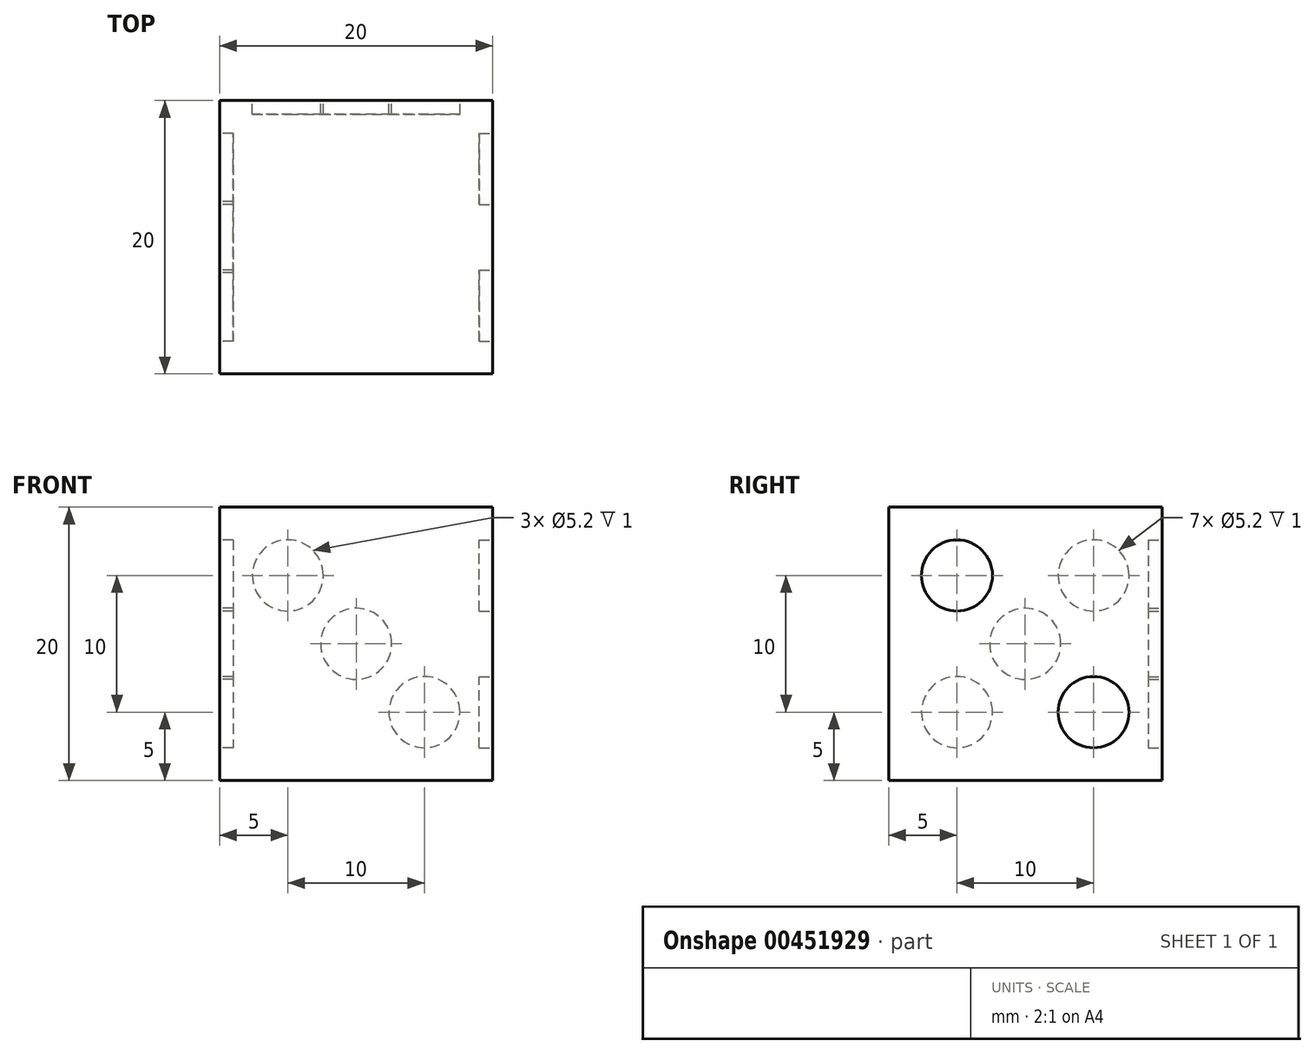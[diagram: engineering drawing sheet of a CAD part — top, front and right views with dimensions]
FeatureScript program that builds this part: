
annotation { "Feature Type Name" : "Feature", "Feature Type Description" : "" }
export const myFeature = defineFeature(function(context is Context, id is Id, definition is map)
    precondition{}
    {
        {
            var Q0;
            Q0=qCreatedBy(makeId("Front.planeOp"),FACE);
            var sketch = newSketch(context, id + "F0", { "sketchPlane" : qUnion([Q0])});
            skLineSegment(sketch, "E0.bottom", {"start": v(0, 0) * mm, "end": v(20, 0) * mm});
            skLineSegment(sketch, "E0.top", {"start": v(0, 20) * mm, "end": v(20, 20) * mm});
            skLineSegment(sketch, "E0.left", {"start": v(0, 0) * mm, "end": v(0, 20) * mm});
            skLineSegment(sketch, "E0.right", {"start": v(20, 0) * mm, "end": v(20, 20) * mm});
            skSolve(sketch);
        }
        {
            var Q0;
            Q0 = qSketchRegion(id + "F0", true);
            extrude(context, id + "F1", {"entities" : qUnion([Q0]), "depth" : 20 * mm});
        }
        {
            var Q0;
            Q0=makeQuery(id+"F1.opExtrude","SWEPT_FACE",FACE,{"disambiguationData":[OSD([sQuery(id+"F0.wireOp",EDGE,"E0.left")])]});
            var sketch = newSketch(context, id + "F2", { "sketchPlane" : qUnion([Q0])});
            skLineSegment(sketch, "E1", {"start": v(0, 20) * mm, "end": v(20, 0) * mm, "construction": true});
            skLineSegment(sketch, "E2", {"start": v(20, 0) * mm, "end": v(20, 20) * mm, "construction": true});
            skLineSegment(sketch, "E3", {"start": v(20, 20) * mm, "end": v(0, 0) * mm, "construction": true});
            skLineSegment(sketch, "E4", {"start": v(0, 10) * mm, "end": v(20, 10) * mm, "construction": true});
            skLineSegment(sketch, "E5", {"start": v(10, 20) * mm, "end": v(10, 0) * mm, "construction": true});
            skCircle(sketch, "E6", {"center": v(10, 10) * mm, "radius": 2.6 * mm});
            skCircle(sketch, "E7", {"center": v(5, 15) * mm, "radius": 2.6 * mm});
            skCircle(sketch, "E8.MirrorC", {"center": v(15, 15) * mm, "radius": 2.6 * mm});
            skCircle(sketch, "E9.MirrorC", {"center": v(15, 5) * mm, "radius": 2.6 * mm});
            skCircle(sketch, "E10.MirrorC", {"center": v(5, 5) * mm, "radius": 2.6 * mm});
            skSolve(sketch);
        }
        {
            var Q0;
            Q0 = qSketchRegion(id + "F2", true);
            extrude(context, id + "F3", {"entities" : qUnion([Q0]), "operationType" : NewBodyOperationType.REMOVE, "oppositeDirection" : true, "depth" : 1 * mm});
        }
        {
            var Q0;
            Q0=makeQuery(id+"F1.opExtrude","SWEPT_FACE",FACE,{"disambiguationData":[OSD([sQuery(id+"F0.wireOp",EDGE,"E0.right")])]});
            var sketch = newSketch(context, id + "F4", { "sketchPlane" : qUnion([Q0])});
            skLineSegment(sketch, "E11", {"start": v(0, 20) * mm, "end": v(-20, 0) * mm, "construction": true});
            skLineSegment(sketch, "E12", {"start": v(-20, 20) * mm, "end": v(0, 0) * mm, "construction": true});
            skLineSegment(sketch, "E13", {"start": v(-10, 20) * mm, "end": v(-10, 0) * mm, "construction": true});
            skLineSegment(sketch, "E14", {"start": v(-20, 10) * mm, "end": v(0, 10) * mm, "construction": true});
            skCircle(sketch, "E15", {"center": v(-15, 15) * mm, "radius": 2.6 * mm});
            skCircle(sketch, "E16.MirrorC", {"center": v(-5, 5) * mm, "radius": 2.6 * mm});
            skSolve(sketch);
        }
        {
            var Q0;
            Q0 = qSketchRegion(id + "F4", true);
            extrude(context, id + "F5", {"entities" : qUnion([Q0]), "operationType" : NewBodyOperationType.REMOVE, "oppositeDirection" : true, "depth" : 1 * mm});
        }
        {
            var Q0;
            Q0=makeQuery(id+"F1.opExtrude","CAP_FACE",FACE,{"disambiguationData":[OSD([sQuery(id+"F0.wireOp",EDGE,"E0.bottom"),sQuery(id+"F0.wireOp",EDGE,"E0.top"),sQuery(id+"F0.wireOp",EDGE,"E0.left"),sQuery(id+"F0.wireOp",EDGE,"E0.right")])],"isStart":true});
            var sketch = newSketch(context, id + "F6", { "sketchPlane" : qUnion([Q0])});
            skLineSegment(sketch, "E17", {"start": v(-10, 20) * mm, "end": v(-10, 0) * mm, "construction": true});
            skLineSegment(sketch, "E18", {"start": v(-20, 10) * mm, "end": v(0, 10) * mm, "construction": true});
            skLineSegment(sketch, "E19", {"start": v(-20, 20) * mm, "end": v(0, 0) * mm, "construction": true});
            skLineSegment(sketch, "E20", {"start": v(0, 20) * mm, "end": v(-20, 0) * mm, "construction": true});
            skCircle(sketch, "E21", {"center": v(-10, 10) * mm, "radius": 2.6 * mm});
            skCircle(sketch, "E22", {"center": v(-5, 15) * mm, "radius": 2.6 * mm});
            skCircle(sketch, "E23.MirrorC", {"center": v(-15, 5) * mm, "radius": 2.6 * mm});
            skSolve(sketch);
        }
        {
            var Q0;
            Q0 = qSketchRegion(id + "F6", true);
            extrude(context, id + "F7", {"entities" : qUnion([Q0]), "operationType" : NewBodyOperationType.REMOVE, "oppositeDirection" : true, "depth" : 1 * mm});
        }
    });
